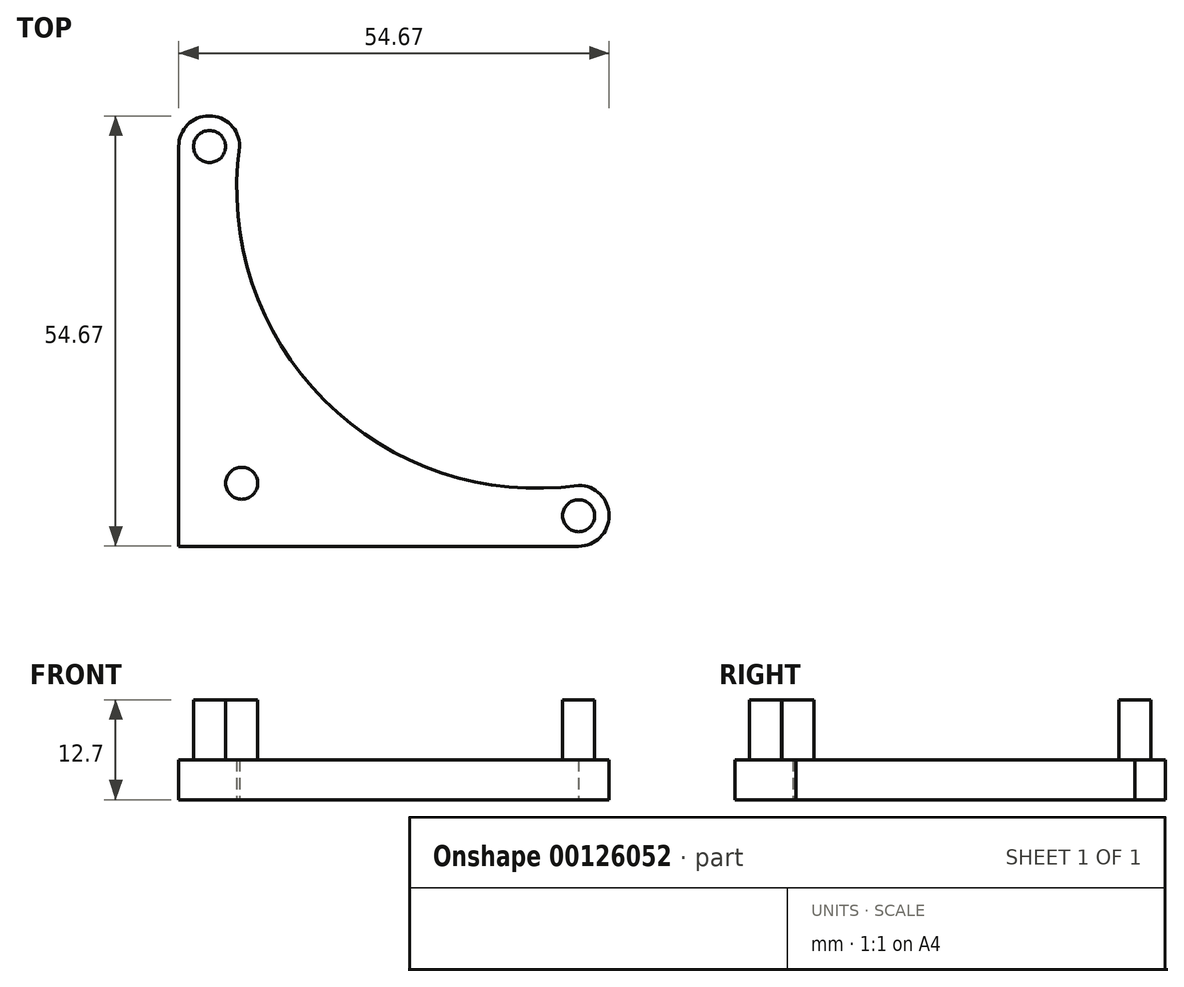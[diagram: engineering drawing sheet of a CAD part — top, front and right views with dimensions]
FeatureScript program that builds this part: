
annotation { "Feature Type Name" : "Feature", "Feature Type Description" : "" }
export const myFeature = defineFeature(function(context is Context, id is Id, definition is map)
    precondition{}
    {
        {
            var Q0;
            Q0=qCreatedBy(makeId("Top.planeOp"),FACE);
            var sketch = newSketch(context, id + "F0", { "sketchPlane" : qUnion([Q0])});
            skLineSegment(sketch, "E0", {"start": v(-35.92, 37.3) * mm, "end": v(-35.92, -13.5) * mm});
            skLineSegment(sketch, "E1", {"start": v(-35.92, -13.5) * mm, "end": v(14.88, -13.5) * mm, "construction": true});
            skArc(sketch, "E2", {"start": v(-28.19, 37.3) * mm, "mid": v(-17.4, 5.03) * mm, "end": v(14.88, -5.76) * mm});
            skArc(sketch, "E3", {"start": v(-28.19, 37.3) * mm, "mid": v(-32.05, 41.18) * mm, "end": v(-35.92, 37.3) * mm});
            skArc(sketch, "E4", {"start": v(14.88, -13.5) * mm, "mid": v(18.75, -9.62) * mm, "end": v(14.88, -5.76) * mm});
            skPoint(sketch, "E5.start.orphan", {"position": v(-159.3, 185.16) * mm});
            skPoint(sketch, "E6.start.orphan", {"position": v(-190.99, 185.16) * mm});
            skPoint(sketch, "E7.end.orphan", {"position": v(129.84, -95.99) * mm});
            skPoint(sketch, "E7.start.orphan", {"position": v(129.84, -134.09) * mm});
            skCircle(sketch, "E8", {"center": v(-27.92, -5.5) * mm, "radius": 2.03 * mm});
            skCircle(sketch, "E9", {"center": v(14.88, -9.62) * mm, "radius": 2.03 * mm});
            skCircle(sketch, "E10", {"center": v(-32, 37.28) * mm, "radius": 2.03 * mm});
            skLineSegment(sketch, "E11", {"start": v(14.88, -13.5) * mm, "end": v(-35.92, -13.5) * mm});
            skLineSegment(sketch, "E12", {"start": v(-27.92, -5.5) * mm, "end": v(-27.92, -7.52) * mm, "construction": true});
            skLineSegment(sketch, "E13", {"start": v(-27.92, -7.52) * mm, "end": v(-27.92, -5.5) * mm, "construction": true});
            skLineSegment(sketch, "E14", {"start": v(-27.92, -5.5) * mm, "end": v(-29.95, -5.5) * mm});
            skLineSegment(sketch, "E15", {"start": v(-29.95, -5.5) * mm, "end": v(-27.92, -5.5) * mm});
            skSolve(sketch);
        }
        {
            var Q0;
            Q0=makeQuery(id+"F0.imprint","IMPRINT",FACE,{"disambiguationData":[TD([[makeQuery(id+"F0.imprint","IMPRINT",EDGE,{"derivedFrom":sQuery(id+"F0.wireOp",EDGE,"E0")}),1.0]])]});
            extrude(context, id + "F1", {"entities" : qUnion([Q0]), "depth" : 5.08 * mm});
        }
        {
            var Q0;
            Q0=makeQuery(id+"F0.imprint","IMPRINT",FACE,{"disambiguationData":[TD([[makeQuery(id+"F0.imprint","IMPRINT",EDGE,{"derivedFrom":sQuery(id+"F0.wireOp",EDGE,"E8")}),1.0]])]});
            var Q1;
            Q1=makeQuery(id+"F0.imprint","IMPRINT",FACE,{"disambiguationData":[TD([[makeQuery(id+"F0.imprint","IMPRINT",EDGE,{"derivedFrom":sQuery(id+"F0.wireOp",EDGE,"E10")}),1.0]])]});
            var Q2;
            Q2=makeQuery(id+"F0.imprint","IMPRINT",FACE,{"disambiguationData":[TD([[makeQuery(id+"F0.imprint","IMPRINT",EDGE,{"derivedFrom":sQuery(id+"F0.wireOp",EDGE,"E9")}),1.0]])]});
            extrude(context, id + "F2", {"entities" : qUnion([Q0, Q1, Q2]), "operationType" : NewBodyOperationType.ADD, "depth" : 12.7 * mm});
        }
    });
